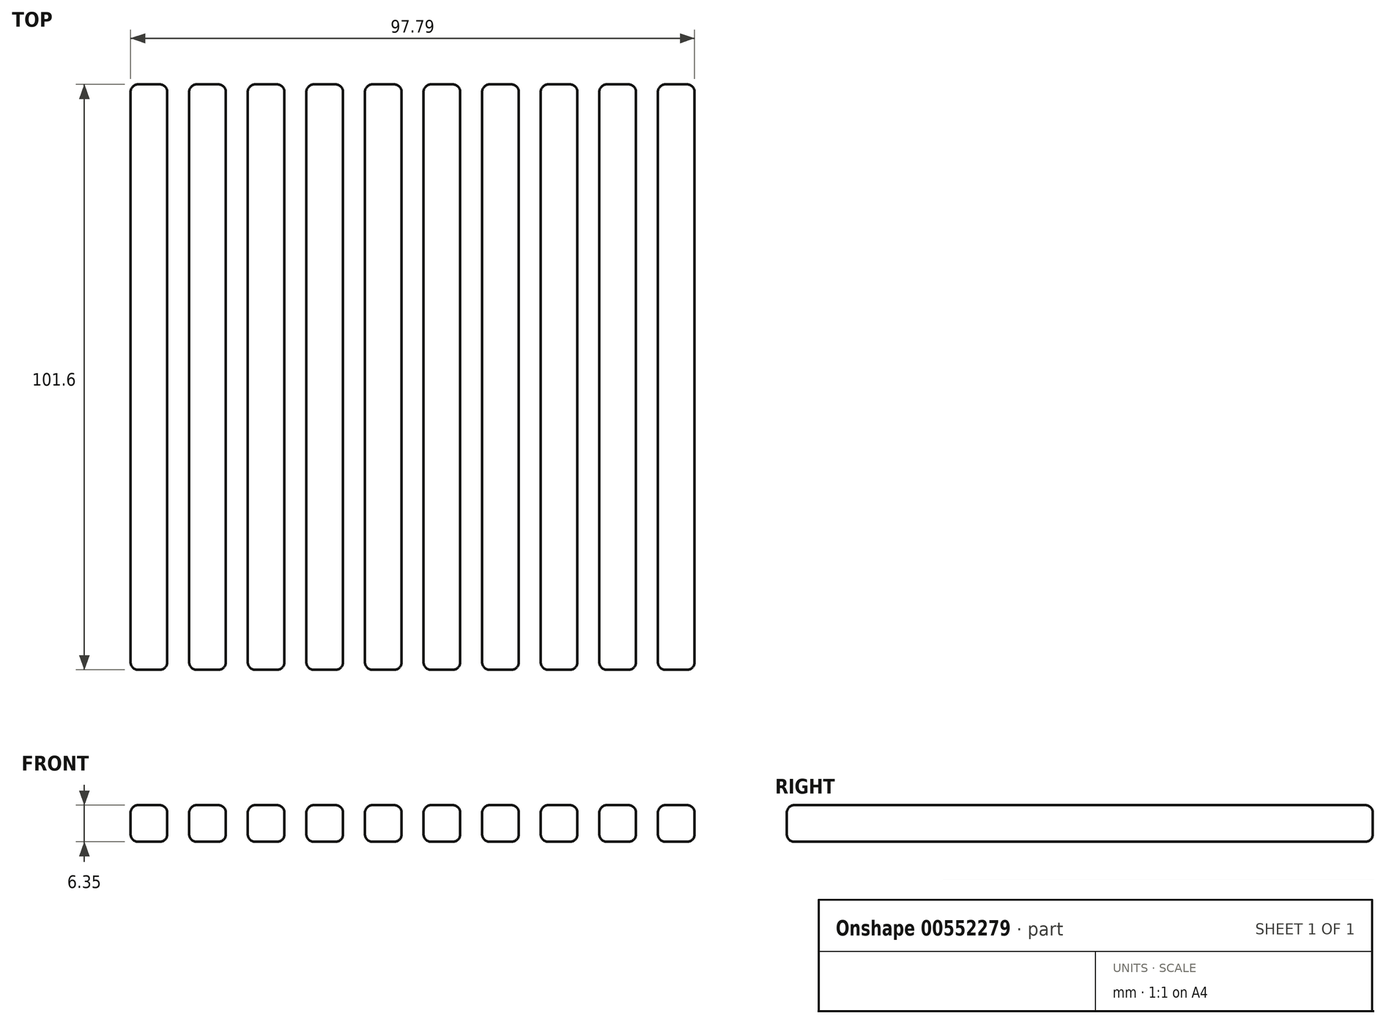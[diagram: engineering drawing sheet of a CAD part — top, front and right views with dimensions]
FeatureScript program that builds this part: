
annotation { "Feature Type Name" : "Feature", "Feature Type Description" : "" }
export const myFeature = defineFeature(function(context is Context, id is Id, definition is map)
    precondition{}
    {
        {
            var Q0;
            Q0=qCreatedBy(makeId("Top.planeOp"),FACE);
            var sketch = newSketch(context, id + "F0", { "sketchPlane" : qUnion([Q0])});
            skLineSegment(sketch, "E0.bottom", {"start": v(0, 0) * mm, "end": v(6.35, 0) * mm});
            skLineSegment(sketch, "E0.top", {"start": v(0, 101.6) * mm, "end": v(6.35, 101.6) * mm});
            skLineSegment(sketch, "E0.left", {"start": v(0, 0) * mm, "end": v(0, 101.6) * mm});
            skLineSegment(sketch, "E0.right", {"start": v(6.35, 0) * mm, "end": v(6.35, 101.6) * mm});
            skLineSegment(sketch, "E1.1.0.0", {"start": v(16.5, 0) * mm, "end": v(16.5, 101.6) * mm});
            skLineSegment(sketch, "E1.1.0.1", {"start": v(10.16, 0) * mm, "end": v(10.16, 101.6) * mm});
            skLineSegment(sketch, "E1.1.0.2", {"start": v(10.16, 101.6) * mm, "end": v(16.5, 101.6) * mm});
            skLineSegment(sketch, "E1.1.0.3", {"start": v(10.16, 0) * mm, "end": v(16.5, 0) * mm});
            skLineSegment(sketch, "E1.2.0.0", {"start": v(26.67, 0) * mm, "end": v(26.67, 101.6) * mm});
            skLineSegment(sketch, "E1.2.0.1", {"start": v(20.32, 0) * mm, "end": v(20.32, 101.6) * mm});
            skLineSegment(sketch, "E1.2.0.2", {"start": v(20.32, 101.6) * mm, "end": v(26.67, 101.6) * mm});
            skLineSegment(sketch, "E1.2.0.3", {"start": v(20.32, 0) * mm, "end": v(26.67, 0) * mm});
            skLineSegment(sketch, "E1.3.0.0", {"start": v(36.83, 0) * mm, "end": v(36.83, 101.6) * mm});
            skLineSegment(sketch, "E1.3.0.1", {"start": v(30.48, 0) * mm, "end": v(30.48, 101.6) * mm});
            skLineSegment(sketch, "E1.3.0.2", {"start": v(30.48, 101.6) * mm, "end": v(36.83, 101.6) * mm});
            skLineSegment(sketch, "E1.3.0.3", {"start": v(30.48, 0) * mm, "end": v(36.83, 0) * mm});
            skLineSegment(sketch, "E1.4.0.0", {"start": v(46.99, 0) * mm, "end": v(46.99, 101.6) * mm});
            skLineSegment(sketch, "E1.4.0.1", {"start": v(40.64, 0) * mm, "end": v(40.64, 101.6) * mm});
            skLineSegment(sketch, "E1.4.0.2", {"start": v(40.64, 101.6) * mm, "end": v(46.99, 101.6) * mm});
            skLineSegment(sketch, "E1.4.0.3", {"start": v(40.64, 0) * mm, "end": v(46.99, 0) * mm});
            skLineSegment(sketch, "E1.5.0.0", {"start": v(57.15, 0) * mm, "end": v(57.15, 101.6) * mm});
            skLineSegment(sketch, "E1.5.0.1", {"start": v(50.8, 0) * mm, "end": v(50.8, 101.6) * mm});
            skLineSegment(sketch, "E1.5.0.2", {"start": v(50.8, 101.6) * mm, "end": v(57.15, 101.6) * mm});
            skLineSegment(sketch, "E1.5.0.3", {"start": v(50.8, 0) * mm, "end": v(57.15, 0) * mm});
            skLineSegment(sketch, "E1.6.0.0", {"start": v(67.3, 0) * mm, "end": v(67.3, 101.6) * mm});
            skLineSegment(sketch, "E1.6.0.1", {"start": v(60.96, 0) * mm, "end": v(60.96, 101.6) * mm});
            skLineSegment(sketch, "E1.6.0.2", {"start": v(60.96, 101.6) * mm, "end": v(67.3, 101.6) * mm});
            skLineSegment(sketch, "E1.6.0.3", {"start": v(60.96, 0) * mm, "end": v(67.3, 0) * mm});
            skLineSegment(sketch, "E1.7.0.0", {"start": v(77.47, 0) * mm, "end": v(77.47, 101.6) * mm});
            skLineSegment(sketch, "E1.7.0.1", {"start": v(71.12, 0) * mm, "end": v(71.12, 101.6) * mm});
            skLineSegment(sketch, "E1.7.0.2", {"start": v(71.12, 101.6) * mm, "end": v(77.47, 101.6) * mm});
            skLineSegment(sketch, "E1.7.0.3", {"start": v(71.12, 0) * mm, "end": v(77.47, 0) * mm});
            skLineSegment(sketch, "E1.8.0.0", {"start": v(87.63, 0) * mm, "end": v(87.63, 101.6) * mm});
            skLineSegment(sketch, "E1.8.0.1", {"start": v(81.28, 0) * mm, "end": v(81.28, 101.6) * mm});
            skLineSegment(sketch, "E1.8.0.2", {"start": v(81.28, 101.6) * mm, "end": v(87.63, 101.6) * mm});
            skLineSegment(sketch, "E1.8.0.3", {"start": v(81.28, 0) * mm, "end": v(87.63, 0) * mm});
            skLineSegment(sketch, "E1.9.0.0", {"start": v(97.8, 0) * mm, "end": v(97.79, 101.6) * mm});
            skLineSegment(sketch, "E1.9.0.1", {"start": v(91.44, 0) * mm, "end": v(91.44, 101.6) * mm});
            skLineSegment(sketch, "E1.9.0.2", {"start": v(91.44, 101.6) * mm, "end": v(97.79, 101.6) * mm});
            skLineSegment(sketch, "E1.9.0.3", {"start": v(91.44, 0) * mm, "end": v(97.8, 0) * mm});
            skLineSegment(sketch, "E1.direction1", {"start": v(0, 0) * mm, "end": v(10.16, 0) * mm, "construction": true});
            skLineSegment(sketch, "E2.direction1", {"start": v(0, 0) * mm, "end": v(25.4, 0) * mm, "construction": true});
            skLineSegment(sketch, "E2.direction2", {"start": v(0, 0) * mm, "end": v(0, 29.46) * mm, "construction": true});
            skSolve(sketch);
        }
        {
            var Q0;
            Q0=qSketchRegion(id+"F0",true);
            extrude(context, id + "F1", {"entities" : qUnion([Q0]), "depth" : 6.35 * mm, "offsetDistance" : 25.4 * mm});
        }
        {
            var Q0;
            Q0=makeQuery(id+"F1.opExtrude","CAP_EDGE",EDGE,{"disambiguationData":[OSD([sQuery(id+"F0.wireOp",EDGE,"E1.9.0.0")])],"isStart":true});
            var Q1;
            Q1=makeQuery(id+"F1.opExtrude","CAP_EDGE",EDGE,{"disambiguationData":[OSD([sQuery(id+"F0.wireOp",EDGE,"E1.9.0.0")])],"isStart":false});
            var Q2;
            Q2=makeQuery(id+"F1.opExtrude","CAP_EDGE",EDGE,{"disambiguationData":[OSD([sQuery(id+"F0.wireOp",EDGE,"E1.9.0.1")])],"isStart":false});
            var Q3;
            Q3=makeQuery(id+"F1.opExtrude","SWEPT_EDGE",EDGE,{"disambiguationData":[OSD([sQuery(id+"F0.wireOp",EDGE,"E1.9.0.0"),sQuery(id+"F0.wireOp",EDGE,"E1.9.0.3")])]});
            var Q4;
            Q4=makeQuery(id+"F1.opExtrude","SWEPT_EDGE",EDGE,{"disambiguationData":[OSD([sQuery(id+"F0.wireOp",EDGE,"E1.9.0.0"),sQuery(id+"F0.wireOp",EDGE,"E1.9.0.2")])]});
            var Q5;
            Q5=makeQuery(id+"F1.opExtrude","SWEPT_EDGE",EDGE,{"disambiguationData":[OSD([sQuery(id+"F0.wireOp",EDGE,"E1.9.0.1"),sQuery(id+"F0.wireOp",EDGE,"E1.9.0.3")])]});
            var Q6;
            Q6=makeQuery(id+"F1.opExtrude","SWEPT_FACE",FACE,{"disambiguationData":[OSD([sQuery(id+"F0.wireOp",EDGE,"E1.9.0.0")])]});
            var Q7;
            Q7=makeQuery(id+"F1.opExtrude","CAP_EDGE",EDGE,{"disambiguationData":[OSD([sQuery(id+"F0.wireOp",EDGE,"E1.9.0.3")])],"isStart":false});
            var Q8;
            Q8=makeQuery(id+"F1.opExtrude","CAP_FACE",FACE,{"disambiguationData":[OSD([sQuery(id+"F0.wireOp",EDGE,"E1.9.0.0"),sQuery(id+"F0.wireOp",EDGE,"E1.9.0.1"),sQuery(id+"F0.wireOp",EDGE,"E1.9.0.2"),sQuery(id+"F0.wireOp",EDGE,"E1.9.0.3")])],"isStart":true});
            var Q9;
            Q9=makeQuery(id+"F1.opExtrude","CAP_FACE",FACE,{"disambiguationData":[OSD([sQuery(id+"F0.wireOp",EDGE,"E1.9.0.0"),sQuery(id+"F0.wireOp",EDGE,"E1.9.0.1"),sQuery(id+"F0.wireOp",EDGE,"E1.9.0.2"),sQuery(id+"F0.wireOp",EDGE,"E1.9.0.3")])],"isStart":false});
            var Q10;
            Q10=makeQuery(id+"F1.opExtrude","SWEPT_FACE",FACE,{"disambiguationData":[OSD([sQuery(id+"F0.wireOp",EDGE,"E1.9.0.1")])]});
            var Q11;
            Q11=makeQuery(id+"F1.opExtrude","SWEPT_FACE",FACE,{"disambiguationData":[OSD([sQuery(id+"F0.wireOp",EDGE,"E1.9.0.2")])]});
            var Q12;
            Q12=makeQuery(id+"F1.opExtrude","SWEPT_FACE",FACE,{"disambiguationData":[OSD([sQuery(id+"F0.wireOp",EDGE,"E1.9.0.3")])]});
            var Q13;
            Q13=makeQuery(id+"F1.opExtrude","SWEPT_EDGE",EDGE,{"disambiguationData":[OSD([sQuery(id+"F0.wireOp",EDGE,"E0.top"),sQuery(id+"F0.wireOp",EDGE,"E0.left")])]});
            var Q14;
            Q14=makeQuery(id+"F1.opExtrude","SWEPT_EDGE",EDGE,{"disambiguationData":[OSD([sQuery(id+"F0.wireOp",EDGE,"E0.top"),sQuery(id+"F0.wireOp",EDGE,"E0.right")])]});
            var Q15;
            Q15=makeQuery(id+"F1.opExtrude","SWEPT_FACE",FACE,{"disambiguationData":[OSD([sQuery(id+"F0.wireOp",EDGE,"E0.top")])]});
            var Q16;
            Q16=makeQuery(id+"F1.opExtrude","SWEPT_EDGE",EDGE,{"disambiguationData":[OSD([sQuery(id+"F0.wireOp",EDGE,"E1.1.0.0"),sQuery(id+"F0.wireOp",EDGE,"E1.1.0.3")])]});
            var Q17;
            Q17=makeQuery(id+"F1.opExtrude","SWEPT_EDGE",EDGE,{"disambiguationData":[OSD([sQuery(id+"F0.wireOp",EDGE,"E1.1.0.0"),sQuery(id+"F0.wireOp",EDGE,"E1.1.0.2")])]});
            var Q18;
            Q18=makeQuery(id+"F1.opExtrude","SWEPT_FACE",FACE,{"disambiguationData":[OSD([sQuery(id+"F0.wireOp",EDGE,"E1.1.0.0")])]});
            var Q19;
            Q19=makeQuery(id+"F1.opExtrude","SWEPT_EDGE",EDGE,{"disambiguationData":[OSD([sQuery(id+"F0.wireOp",EDGE,"E1.1.0.1"),sQuery(id+"F0.wireOp",EDGE,"E1.1.0.2")])]});
            var Q20;
            Q20=makeQuery(id+"F1.opExtrude","SWEPT_FACE",FACE,{"disambiguationData":[OSD([sQuery(id+"F0.wireOp",EDGE,"E1.1.0.2")])]});
            var Q21;
            Q21=makeQuery(id+"F1.opExtrude","CAP_EDGE",EDGE,{"disambiguationData":[OSD([sQuery(id+"F0.wireOp",EDGE,"E1.1.0.0")])],"isStart":false});
            var Q22;
            Q22=makeQuery(id+"F1.opExtrude","SWEPT_FACE",FACE,{"disambiguationData":[OSD([sQuery(id+"F0.wireOp",EDGE,"E1.2.0.1")])]});
            var Q23;
            Q23=makeQuery(id+"F1.opExtrude","CAP_FACE",FACE,{"disambiguationData":[OSD([sQuery(id+"F0.wireOp",EDGE,"E1.2.0.0"),sQuery(id+"F0.wireOp",EDGE,"E1.2.0.1"),sQuery(id+"F0.wireOp",EDGE,"E1.2.0.2"),sQuery(id+"F0.wireOp",EDGE,"E1.2.0.3")])],"isStart":true});
            var Q24;
            Q24=makeQuery(id+"F1.opExtrude","CAP_FACE",FACE,{"disambiguationData":[OSD([sQuery(id+"F0.wireOp",EDGE,"E1.2.0.0"),sQuery(id+"F0.wireOp",EDGE,"E1.2.0.1"),sQuery(id+"F0.wireOp",EDGE,"E1.2.0.2"),sQuery(id+"F0.wireOp",EDGE,"E1.2.0.3")])],"isStart":false});
            var Q25;
            Q25=makeQuery(id+"F1.opExtrude","SWEPT_EDGE",EDGE,{"disambiguationData":[OSD([sQuery(id+"F0.wireOp",EDGE,"E1.2.0.0"),sQuery(id+"F0.wireOp",EDGE,"E1.2.0.3")])]});
            var Q26;
            Q26=makeQuery(id+"F1.opExtrude","SWEPT_EDGE",EDGE,{"disambiguationData":[OSD([sQuery(id+"F0.wireOp",EDGE,"E1.2.0.0"),sQuery(id+"F0.wireOp",EDGE,"E1.2.0.2")])]});
            var Q27;
            Q27=makeQuery(id+"F1.opExtrude","SWEPT_EDGE",EDGE,{"disambiguationData":[OSD([sQuery(id+"F0.wireOp",EDGE,"E1.2.0.1"),sQuery(id+"F0.wireOp",EDGE,"E1.2.0.3")])]});
            var Q28;
            Q28=makeQuery(id+"F1.opExtrude","SWEPT_FACE",FACE,{"disambiguationData":[OSD([sQuery(id+"F0.wireOp",EDGE,"E1.2.0.0")])]});
            var Q29;
            Q29=makeQuery(id+"F1.opExtrude","CAP_EDGE",EDGE,{"disambiguationData":[OSD([sQuery(id+"F0.wireOp",EDGE,"E1.2.0.3")])],"isStart":true});
            var Q30;
            Q30=makeQuery(id+"F1.opExtrude","SWEPT_FACE",FACE,{"disambiguationData":[OSD([sQuery(id+"F0.wireOp",EDGE,"E1.2.0.2")])]});
            var Q31;
            Q31=makeQuery(id+"F1.opExtrude","SWEPT_FACE",FACE,{"disambiguationData":[OSD([sQuery(id+"F0.wireOp",EDGE,"E1.2.0.3")])]});
            var Q32;
            Q32=makeQuery(id+"F1.opExtrude","CAP_EDGE",EDGE,{"disambiguationData":[OSD([sQuery(id+"F0.wireOp",EDGE,"E1.2.0.0")])],"isStart":false});
            var Q33;
            Q33=makeQuery(id+"F1.opExtrude","CAP_EDGE",EDGE,{"disambiguationData":[OSD([sQuery(id+"F0.wireOp",EDGE,"E1.2.0.1")])],"isStart":false});
            var Q34;
            Q34=makeQuery(id+"F1.opExtrude","SWEPT_EDGE",EDGE,{"disambiguationData":[OSD([sQuery(id+"F0.wireOp",EDGE,"E1.3.0.0"),sQuery(id+"F0.wireOp",EDGE,"E1.3.0.2")])]});
            var Q35;
            Q35=makeQuery(id+"F1.opExtrude","SWEPT_EDGE",EDGE,{"disambiguationData":[OSD([sQuery(id+"F0.wireOp",EDGE,"E1.3.0.1"),sQuery(id+"F0.wireOp",EDGE,"E1.3.0.3")])]});
            var Q36;
            Q36=makeQuery(id+"F1.opExtrude","SWEPT_EDGE",EDGE,{"disambiguationData":[OSD([sQuery(id+"F0.wireOp",EDGE,"E1.3.0.0"),sQuery(id+"F0.wireOp",EDGE,"E1.3.0.3")])]});
            var Q37;
            Q37=makeQuery(id+"F1.opExtrude","CAP_EDGE",EDGE,{"disambiguationData":[OSD([sQuery(id+"F0.wireOp",EDGE,"E1.3.0.0")])],"isStart":false});
            var Q38;
            Q38=makeQuery(id+"F1.opExtrude","SWEPT_FACE",FACE,{"disambiguationData":[OSD([sQuery(id+"F0.wireOp",EDGE,"E1.3.0.0")])]});
            var Q39;
            Q39=makeQuery(id+"F1.opExtrude","CAP_EDGE",EDGE,{"disambiguationData":[OSD([sQuery(id+"F0.wireOp",EDGE,"E1.3.0.1")])],"isStart":false});
            var Q40;
            Q40=makeQuery(id+"F1.opExtrude","CAP_FACE",FACE,{"disambiguationData":[OSD([sQuery(id+"F0.wireOp",EDGE,"E1.3.0.0"),sQuery(id+"F0.wireOp",EDGE,"E1.3.0.1"),sQuery(id+"F0.wireOp",EDGE,"E1.3.0.2"),sQuery(id+"F0.wireOp",EDGE,"E1.3.0.3")])],"isStart":true});
            var Q41;
            Q41=makeQuery(id+"F1.opExtrude","CAP_FACE",FACE,{"disambiguationData":[OSD([sQuery(id+"F0.wireOp",EDGE,"E1.3.0.0"),sQuery(id+"F0.wireOp",EDGE,"E1.3.0.1"),sQuery(id+"F0.wireOp",EDGE,"E1.3.0.2"),sQuery(id+"F0.wireOp",EDGE,"E1.3.0.3")])],"isStart":false});
            var Q42;
            Q42=makeQuery(id+"F1.opExtrude","CAP_EDGE",EDGE,{"disambiguationData":[OSD([sQuery(id+"F0.wireOp",EDGE,"E1.3.0.2")])],"isStart":false});
            var Q43;
            Q43=makeQuery(id+"F1.opExtrude","SWEPT_FACE",FACE,{"disambiguationData":[OSD([sQuery(id+"F0.wireOp",EDGE,"E1.3.0.1")])]});
            var Q44;
            Q44=makeQuery(id+"F1.opExtrude","SWEPT_FACE",FACE,{"disambiguationData":[OSD([sQuery(id+"F0.wireOp",EDGE,"E1.3.0.2")])]});
            var Q45;
            Q45=makeQuery(id+"F1.opExtrude","SWEPT_FACE",FACE,{"disambiguationData":[OSD([sQuery(id+"F0.wireOp",EDGE,"E1.3.0.3")])]});
            var Q46;
            Q46=makeQuery(id+"F1.opExtrude","SWEPT_FACE",FACE,{"disambiguationData":[OSD([sQuery(id+"F0.wireOp",EDGE,"E1.4.0.3")])]});
            var Q47;
            Q47=makeQuery(id+"F1.opExtrude","CAP_EDGE",EDGE,{"disambiguationData":[OSD([sQuery(id+"F0.wireOp",EDGE,"E1.4.0.3")])],"isStart":false});
            var Q48;
            Q48=makeQuery(id+"F1.opExtrude","SWEPT_EDGE",EDGE,{"disambiguationData":[OSD([sQuery(id+"F0.wireOp",EDGE,"E1.4.0.0"),sQuery(id+"F0.wireOp",EDGE,"E1.4.0.3")])]});
            var Q49;
            Q49=makeQuery(id+"F1.opExtrude","SWEPT_EDGE",EDGE,{"disambiguationData":[OSD([sQuery(id+"F0.wireOp",EDGE,"E1.4.0.0"),sQuery(id+"F0.wireOp",EDGE,"E1.4.0.2")])]});
            var Q50;
            Q50=makeQuery(id+"F1.opExtrude","SWEPT_EDGE",EDGE,{"disambiguationData":[OSD([sQuery(id+"F0.wireOp",EDGE,"E1.4.0.1"),sQuery(id+"F0.wireOp",EDGE,"E1.4.0.3")])]});
            var Q51;
            Q51=makeQuery(id+"F1.opExtrude","SWEPT_FACE",FACE,{"disambiguationData":[OSD([sQuery(id+"F0.wireOp",EDGE,"E1.4.0.0")])]});
            var Q52;
            Q52=makeQuery(id+"F1.opExtrude","CAP_EDGE",EDGE,{"disambiguationData":[OSD([sQuery(id+"F0.wireOp",EDGE,"E1.4.0.0")])],"isStart":false});
            var Q53;
            Q53=makeQuery(id+"F1.opExtrude","CAP_FACE",FACE,{"disambiguationData":[OSD([sQuery(id+"F0.wireOp",EDGE,"E1.4.0.0"),sQuery(id+"F0.wireOp",EDGE,"E1.4.0.1"),sQuery(id+"F0.wireOp",EDGE,"E1.4.0.2"),sQuery(id+"F0.wireOp",EDGE,"E1.4.0.3")])],"isStart":true});
            var Q54;
            Q54=makeQuery(id+"F1.opExtrude","CAP_FACE",FACE,{"disambiguationData":[OSD([sQuery(id+"F0.wireOp",EDGE,"E1.4.0.0"),sQuery(id+"F0.wireOp",EDGE,"E1.4.0.1"),sQuery(id+"F0.wireOp",EDGE,"E1.4.0.2"),sQuery(id+"F0.wireOp",EDGE,"E1.4.0.3")])],"isStart":false});
            var Q55;
            Q55=makeQuery(id+"F1.opExtrude","CAP_EDGE",EDGE,{"disambiguationData":[OSD([sQuery(id+"F0.wireOp",EDGE,"E1.4.0.1")])],"isStart":false});
            var Q56;
            Q56=makeQuery(id+"F1.opExtrude","SWEPT_FACE",FACE,{"disambiguationData":[OSD([sQuery(id+"F0.wireOp",EDGE,"E1.4.0.1")])]});
            var Q57;
            Q57=makeQuery(id+"F1.opExtrude","SWEPT_FACE",FACE,{"disambiguationData":[OSD([sQuery(id+"F0.wireOp",EDGE,"E1.4.0.2")])]});
            var Q58;
            Q58=makeQuery(id+"F1.opExtrude","CAP_FACE",FACE,{"disambiguationData":[OSD([sQuery(id+"F0.wireOp",EDGE,"E1.5.0.0"),sQuery(id+"F0.wireOp",EDGE,"E1.5.0.1"),sQuery(id+"F0.wireOp",EDGE,"E1.5.0.2"),sQuery(id+"F0.wireOp",EDGE,"E1.5.0.3")])],"isStart":true});
            var Q59;
            Q59=makeQuery(id+"F1.opExtrude","SWEPT_FACE",FACE,{"disambiguationData":[OSD([sQuery(id+"F0.wireOp",EDGE,"E1.5.0.0")])]});
            var Q60;
            Q60=makeQuery(id+"F1.opExtrude","CAP_FACE",FACE,{"disambiguationData":[OSD([sQuery(id+"F0.wireOp",EDGE,"E1.5.0.0"),sQuery(id+"F0.wireOp",EDGE,"E1.5.0.1"),sQuery(id+"F0.wireOp",EDGE,"E1.5.0.2"),sQuery(id+"F0.wireOp",EDGE,"E1.5.0.3")])],"isStart":false});
            var Q61;
            Q61=makeQuery(id+"F1.opExtrude","CAP_EDGE",EDGE,{"disambiguationData":[OSD([sQuery(id+"F0.wireOp",EDGE,"E1.5.0.0")])],"isStart":false});
            var Q62;
            Q62=makeQuery(id+"F1.opExtrude","SWEPT_FACE",FACE,{"disambiguationData":[OSD([sQuery(id+"F0.wireOp",EDGE,"E1.5.0.2")])]});
            var Q63;
            Q63=makeQuery(id+"F1.opExtrude","CAP_EDGE",EDGE,{"disambiguationData":[OSD([sQuery(id+"F0.wireOp",EDGE,"E1.5.0.1")])],"isStart":false});
            var Q64;
            Q64=makeQuery(id+"F1.opExtrude","SWEPT_FACE",FACE,{"disambiguationData":[OSD([sQuery(id+"F0.wireOp",EDGE,"E1.5.0.3")])]});
            var Q65;
            Q65=makeQuery(id+"F1.opExtrude","SWEPT_EDGE",EDGE,{"disambiguationData":[OSD([sQuery(id+"F0.wireOp",EDGE,"E1.5.0.0"),sQuery(id+"F0.wireOp",EDGE,"E1.5.0.3")])]});
            var Q66;
            Q66=makeQuery(id+"F1.opExtrude","SWEPT_EDGE",EDGE,{"disambiguationData":[OSD([sQuery(id+"F0.wireOp",EDGE,"E1.5.0.0"),sQuery(id+"F0.wireOp",EDGE,"E1.5.0.2")])]});
            var Q67;
            Q67=makeQuery(id+"F1.opExtrude","SWEPT_EDGE",EDGE,{"disambiguationData":[OSD([sQuery(id+"F0.wireOp",EDGE,"E1.5.0.1"),sQuery(id+"F0.wireOp",EDGE,"E1.5.0.3")])]});
            var Q68;
            Q68=makeQuery(id+"F1.opExtrude","CAP_EDGE",EDGE,{"disambiguationData":[OSD([sQuery(id+"F0.wireOp",EDGE,"E1.5.0.3")])],"isStart":true});
            var Q69;
            Q69=makeQuery(id+"F1.opExtrude","CAP_EDGE",EDGE,{"disambiguationData":[OSD([sQuery(id+"F0.wireOp",EDGE,"E1.6.0.2")])],"isStart":false});
            var Q70;
            Q70=makeQuery(id+"F1.opExtrude","SWEPT_FACE",FACE,{"disambiguationData":[OSD([sQuery(id+"F0.wireOp",EDGE,"E1.6.0.0")])]});
            var Q71;
            Q71=makeQuery(id+"F1.opExtrude","CAP_FACE",FACE,{"disambiguationData":[OSD([sQuery(id+"F0.wireOp",EDGE,"E1.6.0.0"),sQuery(id+"F0.wireOp",EDGE,"E1.6.0.1"),sQuery(id+"F0.wireOp",EDGE,"E1.6.0.2"),sQuery(id+"F0.wireOp",EDGE,"E1.6.0.3")])],"isStart":true});
            var Q72;
            Q72=makeQuery(id+"F1.opExtrude","CAP_FACE",FACE,{"disambiguationData":[OSD([sQuery(id+"F0.wireOp",EDGE,"E1.6.0.0"),sQuery(id+"F0.wireOp",EDGE,"E1.6.0.1"),sQuery(id+"F0.wireOp",EDGE,"E1.6.0.2"),sQuery(id+"F0.wireOp",EDGE,"E1.6.0.3")])],"isStart":false});
            var Q73;
            Q73=makeQuery(id+"F1.opExtrude","SWEPT_FACE",FACE,{"disambiguationData":[OSD([sQuery(id+"F0.wireOp",EDGE,"E1.6.0.1")])]});
            var Q74;
            Q74=makeQuery(id+"F1.opExtrude","SWEPT_EDGE",EDGE,{"disambiguationData":[OSD([sQuery(id+"F0.wireOp",EDGE,"E1.6.0.0"),sQuery(id+"F0.wireOp",EDGE,"E1.6.0.3")])]});
            var Q75;
            Q75=makeQuery(id+"F1.opExtrude","SWEPT_FACE",FACE,{"disambiguationData":[OSD([sQuery(id+"F0.wireOp",EDGE,"E1.6.0.2")])]});
            var Q76;
            Q76=makeQuery(id+"F1.opExtrude","SWEPT_EDGE",EDGE,{"disambiguationData":[OSD([sQuery(id+"F0.wireOp",EDGE,"E1.6.0.0"),sQuery(id+"F0.wireOp",EDGE,"E1.6.0.2")])]});
            var Q77;
            Q77=makeQuery(id+"F1.opExtrude","CAP_EDGE",EDGE,{"disambiguationData":[OSD([sQuery(id+"F0.wireOp",EDGE,"E1.6.0.0")])],"isStart":false});
            var Q78;
            Q78=makeQuery(id+"F1.opExtrude","SWEPT_FACE",FACE,{"disambiguationData":[OSD([sQuery(id+"F0.wireOp",EDGE,"E1.6.0.3")])]});
            var Q79;
            Q79=makeQuery(id+"F1.opExtrude","SWEPT_EDGE",EDGE,{"disambiguationData":[OSD([sQuery(id+"F0.wireOp",EDGE,"E1.6.0.1"),sQuery(id+"F0.wireOp",EDGE,"E1.6.0.3")])]});
            var Q80;
            Q80=makeQuery(id+"F1.opExtrude","CAP_EDGE",EDGE,{"disambiguationData":[OSD([sQuery(id+"F0.wireOp",EDGE,"E1.6.0.1")])],"isStart":false});
            var Q81;
            Q81=makeQuery(id+"F1.opExtrude","SWEPT_FACE",FACE,{"disambiguationData":[OSD([sQuery(id+"F0.wireOp",EDGE,"E1.7.0.3")])]});
            var Q82;
            Q82=makeQuery(id+"F1.opExtrude","SWEPT_EDGE",EDGE,{"disambiguationData":[OSD([sQuery(id+"F0.wireOp",EDGE,"E1.7.0.0"),sQuery(id+"F0.wireOp",EDGE,"E1.7.0.2")])]});
            var Q83;
            Q83=makeQuery(id+"F1.opExtrude","SWEPT_FACE",FACE,{"disambiguationData":[OSD([sQuery(id+"F0.wireOp",EDGE,"E1.7.0.1")])]});
            var Q84;
            Q84=makeQuery(id+"F1.opExtrude","SWEPT_EDGE",EDGE,{"disambiguationData":[OSD([sQuery(id+"F0.wireOp",EDGE,"E1.7.0.1"),sQuery(id+"F0.wireOp",EDGE,"E1.7.0.3")])]});
            var Q85;
            Q85=makeQuery(id+"F1.opExtrude","SWEPT_FACE",FACE,{"disambiguationData":[OSD([sQuery(id+"F0.wireOp",EDGE,"E1.7.0.2")])]});
            var Q86;
            Q86=makeQuery(id+"F1.opExtrude","CAP_EDGE",EDGE,{"disambiguationData":[OSD([sQuery(id+"F0.wireOp",EDGE,"E1.7.0.0")])],"isStart":false});
            var Q87;
            Q87=makeQuery(id+"F1.opExtrude","CAP_EDGE",EDGE,{"disambiguationData":[OSD([sQuery(id+"F0.wireOp",EDGE,"E1.7.0.1")])],"isStart":false});
            var Q88;
            Q88=makeQuery(id+"F1.opExtrude","CAP_EDGE",EDGE,{"disambiguationData":[OSD([sQuery(id+"F0.wireOp",EDGE,"E1.7.0.3")])],"isStart":true});
            var Q89;
            Q89=makeQuery(id+"F1.opExtrude","SWEPT_FACE",FACE,{"disambiguationData":[OSD([sQuery(id+"F0.wireOp",EDGE,"E1.7.0.0")])]});
            var Q90;
            Q90=makeQuery(id+"F1.opExtrude","CAP_FACE",FACE,{"disambiguationData":[OSD([sQuery(id+"F0.wireOp",EDGE,"E1.7.0.0"),sQuery(id+"F0.wireOp",EDGE,"E1.7.0.1"),sQuery(id+"F0.wireOp",EDGE,"E1.7.0.2"),sQuery(id+"F0.wireOp",EDGE,"E1.7.0.3")])],"isStart":true});
            var Q91;
            Q91=makeQuery(id+"F1.opExtrude","SWEPT_EDGE",EDGE,{"disambiguationData":[OSD([sQuery(id+"F0.wireOp",EDGE,"E1.7.0.0"),sQuery(id+"F0.wireOp",EDGE,"E1.7.0.3")])]});
            var Q92;
            Q92=makeQuery(id+"F1.opExtrude","CAP_FACE",FACE,{"disambiguationData":[OSD([sQuery(id+"F0.wireOp",EDGE,"E1.7.0.0"),sQuery(id+"F0.wireOp",EDGE,"E1.7.0.1"),sQuery(id+"F0.wireOp",EDGE,"E1.7.0.2"),sQuery(id+"F0.wireOp",EDGE,"E1.7.0.3")])],"isStart":false});
            var Q93;
            Q93=makeQuery(id+"F1.opExtrude","CAP_EDGE",EDGE,{"disambiguationData":[OSD([sQuery(id+"F0.wireOp",EDGE,"E1.8.0.2")])],"isStart":false});
            var Q94;
            Q94=makeQuery(id+"F1.opExtrude","SWEPT_EDGE",EDGE,{"disambiguationData":[OSD([sQuery(id+"F0.wireOp",EDGE,"E1.8.0.0"),sQuery(id+"F0.wireOp",EDGE,"E1.8.0.3")])]});
            var Q95;
            Q95=makeQuery(id+"F1.opExtrude","SWEPT_FACE",FACE,{"disambiguationData":[OSD([sQuery(id+"F0.wireOp",EDGE,"E1.8.0.0")])]});
            var Q96;
            Q96=makeQuery(id+"F1.opExtrude","SWEPT_EDGE",EDGE,{"disambiguationData":[OSD([sQuery(id+"F0.wireOp",EDGE,"E1.8.0.0"),sQuery(id+"F0.wireOp",EDGE,"E1.8.0.2")])]});
            var Q97;
            Q97=makeQuery(id+"F1.opExtrude","CAP_FACE",FACE,{"disambiguationData":[OSD([sQuery(id+"F0.wireOp",EDGE,"E1.8.0.0"),sQuery(id+"F0.wireOp",EDGE,"E1.8.0.1"),sQuery(id+"F0.wireOp",EDGE,"E1.8.0.2"),sQuery(id+"F0.wireOp",EDGE,"E1.8.0.3")])],"isStart":true});
            var Q98;
            Q98=makeQuery(id+"F1.opExtrude","SWEPT_EDGE",EDGE,{"disambiguationData":[OSD([sQuery(id+"F0.wireOp",EDGE,"E1.8.0.1"),sQuery(id+"F0.wireOp",EDGE,"E1.8.0.3")])]});
            var Q99;
            Q99=makeQuery(id+"F1.opExtrude","CAP_FACE",FACE,{"disambiguationData":[OSD([sQuery(id+"F0.wireOp",EDGE,"E1.8.0.0"),sQuery(id+"F0.wireOp",EDGE,"E1.8.0.1"),sQuery(id+"F0.wireOp",EDGE,"E1.8.0.2"),sQuery(id+"F0.wireOp",EDGE,"E1.8.0.3")])],"isStart":false});
            var Q100;
            Q100=makeQuery(id+"F1.opExtrude","SWEPT_FACE",FACE,{"disambiguationData":[OSD([sQuery(id+"F0.wireOp",EDGE,"E1.8.0.1")])]});
            var Q101;
            Q101=makeQuery(id+"F1.opExtrude","SWEPT_FACE",FACE,{"disambiguationData":[OSD([sQuery(id+"F0.wireOp",EDGE,"E1.8.0.2")])]});
            var Q102;
            Q102=makeQuery(id+"F1.opExtrude","SWEPT_FACE",FACE,{"disambiguationData":[OSD([sQuery(id+"F0.wireOp",EDGE,"E1.8.0.3")])]});
            var Q103;
            Q103=makeQuery(id+"F1.opExtrude","CAP_EDGE",EDGE,{"disambiguationData":[OSD([sQuery(id+"F0.wireOp",EDGE,"E1.8.0.0")])],"isStart":false});
            var Q104;
            Q104=makeQuery(id+"F1.opExtrude","CAP_EDGE",EDGE,{"disambiguationData":[OSD([sQuery(id+"F0.wireOp",EDGE,"E1.8.0.1")])],"isStart":false});
            var Q105;
            Q105=makeQuery(id+"F1.opExtrude","CAP_EDGE",EDGE,{"disambiguationData":[OSD([sQuery(id+"F0.wireOp",EDGE,"E1.9.0.1")])],"isStart":true});
            var Q106;
            Q106=makeQuery(id+"F1.opExtrude","CAP_EDGE",EDGE,{"disambiguationData":[OSD([sQuery(id+"F0.wireOp",EDGE,"E1.9.0.2")])],"isStart":true});
            var Q107;
            Q107=makeQuery(id+"F1.opExtrude","CAP_EDGE",EDGE,{"disambiguationData":[OSD([sQuery(id+"F0.wireOp",EDGE,"E1.9.0.2")])],"isStart":false});
            var Q108;
            Q108=makeQuery(id+"F1.opExtrude","CAP_EDGE",EDGE,{"disambiguationData":[OSD([sQuery(id+"F0.wireOp",EDGE,"E1.9.0.3")])],"isStart":true});
            var Q109;
            Q109=makeQuery(id+"F1.opExtrude","SWEPT_EDGE",EDGE,{"disambiguationData":[OSD([sQuery(id+"F0.wireOp",EDGE,"E1.9.0.1"),sQuery(id+"F0.wireOp",EDGE,"E1.9.0.2")])]});
            var Q110;
            Q110=makeQuery(id+"F1.opExtrude","CAP_EDGE",EDGE,{"disambiguationData":[OSD([sQuery(id+"F0.wireOp",EDGE,"E0.top")])],"isStart":true});
            var Q111;
            Q111=makeQuery(id+"F1.opExtrude","CAP_EDGE",EDGE,{"disambiguationData":[OSD([sQuery(id+"F0.wireOp",EDGE,"E0.top")])],"isStart":false});
            var Q112;
            Q112=makeQuery(id+"F1.opExtrude","CAP_EDGE",EDGE,{"disambiguationData":[OSD([sQuery(id+"F0.wireOp",EDGE,"E1.1.0.0")])],"isStart":true});
            var Q113;
            Q113=makeQuery(id+"F1.opExtrude","CAP_EDGE",EDGE,{"disambiguationData":[OSD([sQuery(id+"F0.wireOp",EDGE,"E1.1.0.2")])],"isStart":true});
            var Q114;
            Q114=makeQuery(id+"F1.opExtrude","CAP_EDGE",EDGE,{"disambiguationData":[OSD([sQuery(id+"F0.wireOp",EDGE,"E1.1.0.2")])],"isStart":false});
            var Q115;
            Q115=makeQuery(id+"F1.opExtrude","SWEPT_EDGE",EDGE,{"disambiguationData":[OSD([sQuery(id+"F0.wireOp",EDGE,"E1.2.0.1"),sQuery(id+"F0.wireOp",EDGE,"E1.2.0.2")])]});
            var Q116;
            Q116=makeQuery(id+"F1.opExtrude","CAP_EDGE",EDGE,{"disambiguationData":[OSD([sQuery(id+"F0.wireOp",EDGE,"E1.2.0.2")])],"isStart":false});
            var Q117;
            Q117=makeQuery(id+"F1.opExtrude","CAP_EDGE",EDGE,{"disambiguationData":[OSD([sQuery(id+"F0.wireOp",EDGE,"E1.2.0.3")])],"isStart":false});
            var Q118;
            Q118=makeQuery(id+"F1.opExtrude","CAP_EDGE",EDGE,{"disambiguationData":[OSD([sQuery(id+"F0.wireOp",EDGE,"E1.2.0.0")])],"isStart":true});
            var Q119;
            Q119=makeQuery(id+"F1.opExtrude","CAP_EDGE",EDGE,{"disambiguationData":[OSD([sQuery(id+"F0.wireOp",EDGE,"E1.2.0.1")])],"isStart":true});
            var Q120;
            Q120=makeQuery(id+"F1.opExtrude","CAP_EDGE",EDGE,{"disambiguationData":[OSD([sQuery(id+"F0.wireOp",EDGE,"E1.2.0.2")])],"isStart":true});
            var Q121;
            Q121=makeQuery(id+"F1.opExtrude","SWEPT_EDGE",EDGE,{"disambiguationData":[OSD([sQuery(id+"F0.wireOp",EDGE,"E1.3.0.1"),sQuery(id+"F0.wireOp",EDGE,"E1.3.0.2")])]});
            var Q122;
            Q122=makeQuery(id+"F1.opExtrude","CAP_EDGE",EDGE,{"disambiguationData":[OSD([sQuery(id+"F0.wireOp",EDGE,"E1.3.0.0")])],"isStart":true});
            var Q123;
            Q123=makeQuery(id+"F1.opExtrude","CAP_EDGE",EDGE,{"disambiguationData":[OSD([sQuery(id+"F0.wireOp",EDGE,"E1.3.0.1")])],"isStart":true});
            var Q124;
            Q124=makeQuery(id+"F1.opExtrude","CAP_EDGE",EDGE,{"disambiguationData":[OSD([sQuery(id+"F0.wireOp",EDGE,"E1.3.0.2")])],"isStart":true});
            var Q125;
            Q125=makeQuery(id+"F1.opExtrude","CAP_EDGE",EDGE,{"disambiguationData":[OSD([sQuery(id+"F0.wireOp",EDGE,"E1.3.0.3")])],"isStart":true});
            var Q126;
            Q126=makeQuery(id+"F1.opExtrude","CAP_EDGE",EDGE,{"disambiguationData":[OSD([sQuery(id+"F0.wireOp",EDGE,"E1.3.0.3")])],"isStart":false});
            var Q127;
            Q127=makeQuery(id+"F1.opExtrude","CAP_EDGE",EDGE,{"disambiguationData":[OSD([sQuery(id+"F0.wireOp",EDGE,"E1.4.0.2")])],"isStart":false});
            var Q128;
            Q128=makeQuery(id+"F1.opExtrude","CAP_EDGE",EDGE,{"disambiguationData":[OSD([sQuery(id+"F0.wireOp",EDGE,"E1.4.0.3")])],"isStart":true});
            var Q129;
            Q129=makeQuery(id+"F1.opExtrude","SWEPT_EDGE",EDGE,{"disambiguationData":[OSD([sQuery(id+"F0.wireOp",EDGE,"E1.4.0.1"),sQuery(id+"F0.wireOp",EDGE,"E1.4.0.2")])]});
            var Q130;
            Q130=makeQuery(id+"F1.opExtrude","CAP_EDGE",EDGE,{"disambiguationData":[OSD([sQuery(id+"F0.wireOp",EDGE,"E1.4.0.0")])],"isStart":true});
            var Q131;
            Q131=makeQuery(id+"F1.opExtrude","CAP_EDGE",EDGE,{"disambiguationData":[OSD([sQuery(id+"F0.wireOp",EDGE,"E1.4.0.1")])],"isStart":true});
            var Q132;
            Q132=makeQuery(id+"F1.opExtrude","CAP_EDGE",EDGE,{"disambiguationData":[OSD([sQuery(id+"F0.wireOp",EDGE,"E1.4.0.2")])],"isStart":true});
            var Q133;
            Q133=makeQuery(id+"F1.opExtrude","CAP_EDGE",EDGE,{"disambiguationData":[OSD([sQuery(id+"F0.wireOp",EDGE,"E1.5.0.0")])],"isStart":true});
            var Q134;
            Q134=makeQuery(id+"F1.opExtrude","SWEPT_FACE",FACE,{"disambiguationData":[OSD([sQuery(id+"F0.wireOp",EDGE,"E1.5.0.1")])]});
            var Q135;
            Q135=makeQuery(id+"F1.opExtrude","CAP_EDGE",EDGE,{"disambiguationData":[OSD([sQuery(id+"F0.wireOp",EDGE,"E1.5.0.1")])],"isStart":true});
            var Q136;
            Q136=makeQuery(id+"F1.opExtrude","CAP_EDGE",EDGE,{"disambiguationData":[OSD([sQuery(id+"F0.wireOp",EDGE,"E1.5.0.2")])],"isStart":true});
            var Q137;
            Q137=makeQuery(id+"F1.opExtrude","CAP_EDGE",EDGE,{"disambiguationData":[OSD([sQuery(id+"F0.wireOp",EDGE,"E1.5.0.2")])],"isStart":false});
            var Q138;
            Q138=makeQuery(id+"F1.opExtrude","SWEPT_EDGE",EDGE,{"disambiguationData":[OSD([sQuery(id+"F0.wireOp",EDGE,"E1.5.0.1"),sQuery(id+"F0.wireOp",EDGE,"E1.5.0.2")])]});
            var Q139;
            Q139=makeQuery(id+"F1.opExtrude","CAP_EDGE",EDGE,{"disambiguationData":[OSD([sQuery(id+"F0.wireOp",EDGE,"E1.5.0.3")])],"isStart":false});
            var Q140;
            Q140=makeQuery(id+"F1.opExtrude","CAP_EDGE",EDGE,{"disambiguationData":[OSD([sQuery(id+"F0.wireOp",EDGE,"E1.6.0.3")])],"isStart":true});
            var Q141;
            Q141=makeQuery(id+"F1.opExtrude","CAP_EDGE",EDGE,{"disambiguationData":[OSD([sQuery(id+"F0.wireOp",EDGE,"E1.6.0.3")])],"isStart":false});
            var Q142;
            Q142=makeQuery(id+"F1.opExtrude","CAP_EDGE",EDGE,{"disambiguationData":[OSD([sQuery(id+"F0.wireOp",EDGE,"E1.6.0.0")])],"isStart":true});
            var Q143;
            Q143=makeQuery(id+"F1.opExtrude","CAP_EDGE",EDGE,{"disambiguationData":[OSD([sQuery(id+"F0.wireOp",EDGE,"E1.6.0.1")])],"isStart":true});
            var Q144;
            Q144=makeQuery(id+"F1.opExtrude","SWEPT_EDGE",EDGE,{"disambiguationData":[OSD([sQuery(id+"F0.wireOp",EDGE,"E1.6.0.1"),sQuery(id+"F0.wireOp",EDGE,"E1.6.0.2")])]});
            var Q145;
            Q145=makeQuery(id+"F1.opExtrude","CAP_EDGE",EDGE,{"disambiguationData":[OSD([sQuery(id+"F0.wireOp",EDGE,"E1.6.0.2")])],"isStart":true});
            var Q146;
            Q146=makeQuery(id+"F1.opExtrude","SWEPT_EDGE",EDGE,{"disambiguationData":[OSD([sQuery(id+"F0.wireOp",EDGE,"E1.7.0.1"),sQuery(id+"F0.wireOp",EDGE,"E1.7.0.2")])]});
            var Q147;
            Q147=makeQuery(id+"F1.opExtrude","CAP_EDGE",EDGE,{"disambiguationData":[OSD([sQuery(id+"F0.wireOp",EDGE,"E1.7.0.0")])],"isStart":true});
            var Q148;
            Q148=makeQuery(id+"F1.opExtrude","CAP_EDGE",EDGE,{"disambiguationData":[OSD([sQuery(id+"F0.wireOp",EDGE,"E1.7.0.1")])],"isStart":true});
            var Q149;
            Q149=makeQuery(id+"F1.opExtrude","CAP_EDGE",EDGE,{"disambiguationData":[OSD([sQuery(id+"F0.wireOp",EDGE,"E1.7.0.2")])],"isStart":true});
            var Q150;
            Q150=makeQuery(id+"F1.opExtrude","CAP_EDGE",EDGE,{"disambiguationData":[OSD([sQuery(id+"F0.wireOp",EDGE,"E1.7.0.2")])],"isStart":false});
            var Q151;
            Q151=makeQuery(id+"F1.opExtrude","CAP_EDGE",EDGE,{"disambiguationData":[OSD([sQuery(id+"F0.wireOp",EDGE,"E1.7.0.3")])],"isStart":false});
            var Q152;
            Q152=makeQuery(id+"F1.opExtrude","CAP_EDGE",EDGE,{"disambiguationData":[OSD([sQuery(id+"F0.wireOp",EDGE,"E1.8.0.3")])],"isStart":true});
            var Q153;
            Q153=makeQuery(id+"F1.opExtrude","CAP_EDGE",EDGE,{"disambiguationData":[OSD([sQuery(id+"F0.wireOp",EDGE,"E1.8.0.3")])],"isStart":false});
            var Q154;
            Q154=makeQuery(id+"F1.opExtrude","SWEPT_EDGE",EDGE,{"disambiguationData":[OSD([sQuery(id+"F0.wireOp",EDGE,"E1.8.0.1"),sQuery(id+"F0.wireOp",EDGE,"E1.8.0.2")])]});
            var Q155;
            Q155=makeQuery(id+"F1.opExtrude","CAP_EDGE",EDGE,{"disambiguationData":[OSD([sQuery(id+"F0.wireOp",EDGE,"E1.8.0.0")])],"isStart":true});
            var Q156;
            Q156=makeQuery(id+"F1.opExtrude","CAP_EDGE",EDGE,{"disambiguationData":[OSD([sQuery(id+"F0.wireOp",EDGE,"E1.8.0.1")])],"isStart":true});
            var Q157;
            Q157=makeQuery(id+"F1.opExtrude","CAP_EDGE",EDGE,{"disambiguationData":[OSD([sQuery(id+"F0.wireOp",EDGE,"E1.8.0.2")])],"isStart":true});
            var Q158;
            Q158=makeQuery(id+"F1.opExtrude","SWEPT_EDGE",EDGE,{"disambiguationData":[OSD([sQuery(id+"F0.wireOp",EDGE,"E0.bottom"),sQuery(id+"F0.wireOp",EDGE,"E0.left")])]});
            var Q159;
            Q159=makeQuery(id+"F1.opExtrude","SWEPT_FACE",FACE,{"disambiguationData":[OSD([sQuery(id+"F0.wireOp",EDGE,"E0.bottom")])]});
            var Q160;
            Q160=makeQuery(id+"F1.opExtrude","SWEPT_EDGE",EDGE,{"disambiguationData":[OSD([sQuery(id+"F0.wireOp",EDGE,"E0.bottom"),sQuery(id+"F0.wireOp",EDGE,"E0.right")])]});
            var Q161;
            Q161=makeQuery(id+"F1.opExtrude","CAP_FACE",FACE,{"disambiguationData":[OSD([sQuery(id+"F0.wireOp",EDGE,"E0.bottom"),sQuery(id+"F0.wireOp",EDGE,"E0.top"),sQuery(id+"F0.wireOp",EDGE,"E0.left"),sQuery(id+"F0.wireOp",EDGE,"E0.right")])],"isStart":false});
            var Q162;
            Q162=makeQuery(id+"F1.opExtrude","CAP_EDGE",EDGE,{"disambiguationData":[OSD([sQuery(id+"F0.wireOp",EDGE,"E0.bottom")])],"isStart":false});
            var Q163;
            Q163=makeQuery(id+"F1.opExtrude","SWEPT_EDGE",EDGE,{"disambiguationData":[OSD([sQuery(id+"F0.wireOp",EDGE,"E1.1.0.1"),sQuery(id+"F0.wireOp",EDGE,"E1.1.0.3")])]});
            var Q164;
            Q164=makeQuery(id+"F1.opExtrude","CAP_FACE",FACE,{"disambiguationData":[OSD([sQuery(id+"F0.wireOp",EDGE,"E1.1.0.0"),sQuery(id+"F0.wireOp",EDGE,"E1.1.0.1"),sQuery(id+"F0.wireOp",EDGE,"E1.1.0.2"),sQuery(id+"F0.wireOp",EDGE,"E1.1.0.3")])],"isStart":true});
            var Q165;
            Q165=makeQuery(id+"F1.opExtrude","CAP_FACE",FACE,{"disambiguationData":[OSD([sQuery(id+"F0.wireOp",EDGE,"E1.1.0.0"),sQuery(id+"F0.wireOp",EDGE,"E1.1.0.1"),sQuery(id+"F0.wireOp",EDGE,"E1.1.0.2"),sQuery(id+"F0.wireOp",EDGE,"E1.1.0.3")])],"isStart":false});
            var Q166;
            Q166=makeQuery(id+"F1.opExtrude","SWEPT_FACE",FACE,{"disambiguationData":[OSD([sQuery(id+"F0.wireOp",EDGE,"E1.1.0.3")])]});
            var Q167;
            Q167=makeQuery(id+"F1.opExtrude","CAP_FACE",FACE,{"disambiguationData":[OSD([sQuery(id+"F0.wireOp",EDGE,"E0.bottom"),sQuery(id+"F0.wireOp",EDGE,"E0.top"),sQuery(id+"F0.wireOp",EDGE,"E0.left"),sQuery(id+"F0.wireOp",EDGE,"E0.right")])],"isStart":true});
            var Q168;
            Q168=makeQuery(id+"F1.opExtrude","SWEPT_FACE",FACE,{"disambiguationData":[OSD([sQuery(id+"F0.wireOp",EDGE,"E0.left")])]});
            var Q169;
            Q169=makeQuery(id+"F1.opExtrude","SWEPT_FACE",FACE,{"disambiguationData":[OSD([sQuery(id+"F0.wireOp",EDGE,"E0.right")])]});
            var Q170;
            Q170=makeQuery(id+"F1.opExtrude","CAP_EDGE",EDGE,{"disambiguationData":[OSD([sQuery(id+"F0.wireOp",EDGE,"E0.left")])],"isStart":false});
            var Q171;
            Q171=makeQuery(id+"F1.opExtrude","CAP_EDGE",EDGE,{"disambiguationData":[OSD([sQuery(id+"F0.wireOp",EDGE,"E0.right")])],"isStart":true});
            var Q172;
            Q172=makeQuery(id+"F1.opExtrude","CAP_EDGE",EDGE,{"disambiguationData":[OSD([sQuery(id+"F0.wireOp",EDGE,"E0.right")])],"isStart":false});
            var Q173;
            Q173=makeQuery(id+"F1.opExtrude","CAP_EDGE",EDGE,{"disambiguationData":[OSD([sQuery(id+"F0.wireOp",EDGE,"E0.left")])],"isStart":true});
            var Q174;
            Q174=makeQuery(id+"F1.opExtrude","SWEPT_FACE",FACE,{"disambiguationData":[OSD([sQuery(id+"F0.wireOp",EDGE,"E1.1.0.1")])]});
            var Q175;
            Q175=makeQuery(id+"F1.opExtrude","CAP_EDGE",EDGE,{"disambiguationData":[OSD([sQuery(id+"F0.wireOp",EDGE,"E1.1.0.1")])],"isStart":true});
            var Q176;
            Q176=makeQuery(id+"F1.opExtrude","CAP_EDGE",EDGE,{"disambiguationData":[OSD([sQuery(id+"F0.wireOp",EDGE,"E1.1.0.1")])],"isStart":false});
            var Q177;
            Q177=makeQuery(id+"F1.opExtrude","CAP_EDGE",EDGE,{"disambiguationData":[OSD([sQuery(id+"F0.wireOp",EDGE,"E1.1.0.3")])],"isStart":true});
            var Q178;
            Q178=makeQuery(id+"F1.opExtrude","CAP_EDGE",EDGE,{"disambiguationData":[OSD([sQuery(id+"F0.wireOp",EDGE,"E1.1.0.3")])],"isStart":false});
            var Q179;
            Q179=makeQuery(id+"F1.opExtrude","CAP_EDGE",EDGE,{"disambiguationData":[OSD([sQuery(id+"F0.wireOp",EDGE,"E0.bottom")])],"isStart":true});
            fillet(context, id + "F2", {"entities" : qUnion([Q0, Q1, Q2, Q3, Q4, Q5, Q6, Q7, Q8, Q9, Q10, Q11, Q12, Q13, Q14, Q15, Q16, Q17, Q18, Q19, Q20, Q21, Q22, Q23, Q24, Q25, Q26, Q27, Q28, Q29, Q30, Q31, Q32, Q33, Q34, Q35, Q36, Q37, Q38, Q39, Q40, Q41, Q42, Q43, Q44, Q45, Q46, Q47, Q48, Q49, Q50, Q51, Q52, Q53, Q54, Q55, Q56, Q57, Q58, Q59, Q60, Q61, Q62, Q63, Q64, Q65, Q66, Q67, Q68, Q69, Q70, Q71, Q72, Q73, Q74, Q75, Q76, Q77, Q78, Q79, Q80, Q81, Q82, Q83, Q84, Q85, Q86, Q87, Q88, Q89, Q90, Q91, Q92, Q93, Q94, Q95, Q96, Q97, Q98, Q99, Q100, Q101, Q102, Q103, Q104, Q105, Q106, Q107, Q108, Q109, Q110, Q111, Q112, Q113, Q114, Q115, Q116, Q117, Q118, Q119, Q120, Q121, Q122, Q123, Q124, Q125, Q126, Q127, Q128, Q129, Q130, Q131, Q132, Q133, Q134, Q135, Q136, Q137, Q138, Q139, Q140, Q141, Q142, Q143, Q144, Q145, Q146, Q147, Q148, Q149, Q150, Q151, Q152, Q153, Q154, Q155, Q156, Q157, Q158, Q159, Q160, Q161, Q162, Q163, Q164, Q165, Q166, Q167, Q168, Q169, Q170, Q171, Q172, Q173, Q174, Q175, Q176, Q177, Q178, Q179]), "radius" : 1.27 * mm, "tangentPropagation" : true, "allowEdgeOverflow" : false});
        }
    });
